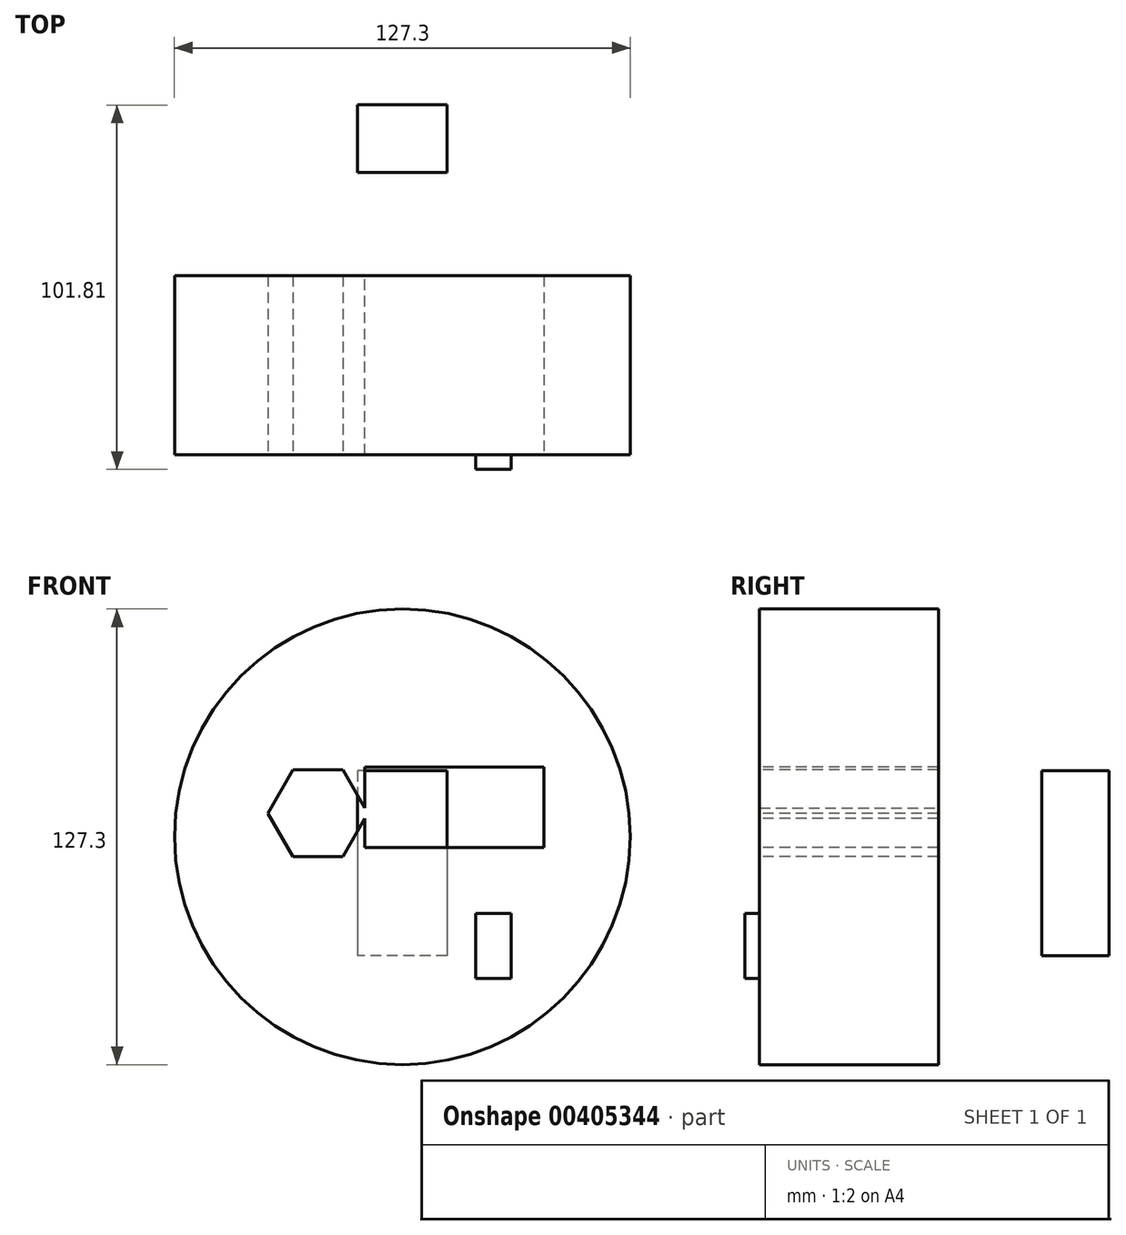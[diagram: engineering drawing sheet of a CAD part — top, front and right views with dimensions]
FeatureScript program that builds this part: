
annotation { "Feature Type Name" : "Feature", "Feature Type Description" : "" }
export const myFeature = defineFeature(function(context is Context, id is Id, definition is map)
    precondition{}
    {
        {
            var Q0;
            Q0=qCreatedBy(makeId("Front.planeOp"),FACE);
            var sketch = newSketch(context, id + "F0", { "sketchPlane" : qUnion([Q0])});
            skCircle(sketch, "E0", {"center": v(0, 0) * mm, "radius": 63.65 * mm});
            skSolve(sketch);
        }
        {
            var Q0;
            Q0=makeQuery(id+"F0.imprint","IMPRINT",FACE,{"disambiguationData":[TD([[makeQuery(id+"F0.imprint","IMPRINT",EDGE,{"derivedFrom":sQuery(id+"F0.wireOp",EDGE,"E0")}),1.0]])]});
            extrude(context, id + "F1", {"entities" : qUnion([Q0]), "endBound" : BoundingType.SYMMETRIC, "depth" : 50 * mm});
        }
        {
            var Q0;
            Q0=makeQuery(id+"F1.opExtrude","CAP_FACE",FACE,{"disambiguationData":[OSD([sQuery(id+"F0.wireOp",EDGE,"E0")])],"isStart":false});
            var sketch = newSketch(context, id + "F2", { "sketchPlane" : qUnion([Q0])});
            skLineSegment(sketch, "E1.bottom", {"start": v(-10.5, 19.5) * mm, "end": v(39.5, 19.5) * mm});
            skLineSegment(sketch, "E1.top", {"start": v(-10.5, -3.05) * mm, "end": v(39.5, -3.05) * mm});
            skLineSegment(sketch, "E1.left", {"start": v(39.5, -3.05) * mm, "end": v(39.5, 19.5) * mm});
            skLineSegment(sketch, "E1.right", {"start": v(-10.5, -3.05) * mm, "end": v(-10.5, 19.5) * mm});
            skPoint(sketch, "E1.middle", {"position": v(14.5, 8.23) * mm});
            skSolve(sketch);
        }
        {
            var Q0;
            Q0=makeQuery(id+"F2.imprint","IMPRINT",FACE,{"disambiguationData":[TD([[makeQuery(id+"F2.imprint","IMPRINT",EDGE,{"derivedFrom":sQuery(id+"F2.wireOp",EDGE,"E1.bottom")}),-1.0]])]});
            extrude(context, id + "F3", {"entities" : qUnion([Q0]), "operationType" : NewBodyOperationType.REMOVE, "oppositeDirection" : true, "depth" : 100 * mm});
        }
        {
            var Q0;
            Q0=makeQuery(id+"F1.opExtrude","CAP_FACE",FACE,{"disambiguationData":[OSD([sQuery(id+"F0.wireOp",EDGE,"E0")])],"isStart":false});
            var sketch = newSketch(context, id + "F4", { "sketchPlane" : qUnion([Q0])});
            skCircle(sketch, "E2.cCircle", {"center": v(-23.62, 6.57) * mm, "radius": 12.11 * mm, "construction": true});
            skLineSegment(sketch, "E2.0", {"start": v(-30.61, 18.68) * mm, "end": v(-16.63, 18.68) * mm});
            skLineSegment(sketch, "E2.1", {"start": v(-16.63, 18.68) * mm, "end": v(-9.64, 6.57) * mm});
            skLineSegment(sketch, "E2.2", {"start": v(-9.64, 6.57) * mm, "end": v(-16.63, -5.54) * mm});
            skLineSegment(sketch, "E2.3", {"start": v(-16.63, -5.54) * mm, "end": v(-30.61, -5.54) * mm});
            skLineSegment(sketch, "E2.4", {"start": v(-30.61, -5.54) * mm, "end": v(-37.6, 6.57) * mm});
            skLineSegment(sketch, "E2.5", {"start": v(-37.6, 6.57) * mm, "end": v(-30.61, 18.68) * mm});
            skPoint(sketch, "E2.0.midPoint", {"position": v(-23.62, 18.68) * mm});
            skSolve(sketch);
        }
        {
            var Q0;
            Q0 = qSketchRegion(id + "F4", true);
            extrude(context, id + "F5", {"entities" : qUnion([Q0]), "operationType" : NewBodyOperationType.REMOVE, "oppositeDirection" : true, "depth" : 60 * mm});
        }
        {
            var Q0;
            Q0=makeQuery(id+"F1.opExtrude","CAP_FACE",FACE,{"disambiguationData":[OSD([sQuery(id+"F0.wireOp",EDGE,"E0")])],"isStart":false});
            var sketch = newSketch(context, id + "F6", { "sketchPlane" : qUnion([Q0])});
            skLineSegment(sketch, "E3.bottom", {"start": v(30.34, -39.6) * mm, "end": v(20.49, -39.6) * mm});
            skLineSegment(sketch, "E3.top", {"start": v(30.34, -21.43) * mm, "end": v(20.49, -21.43) * mm});
            skLineSegment(sketch, "E3.left", {"start": v(30.34, -39.6) * mm, "end": v(30.34, -21.43) * mm});
            skLineSegment(sketch, "E3.right", {"start": v(20.49, -39.6) * mm, "end": v(20.49, -21.43) * mm});
            skPoint(sketch, "E4.firstSnap0", {"position": v(30.34, -30.5) * mm});
            skPoint(sketch, "E4.oppositeSnap0", {"position": v(30.34, -30.5) * mm});
            skSolve(sketch);
        }
        {
            var Q0;
            Q0=makeQuery(id+"F6.imprint","IMPRINT",FACE,{"disambiguationData":[TD([[makeQuery(id+"F6.imprint","IMPRINT",EDGE,{"derivedFrom":sQuery(id+"F6.wireOp",EDGE,"E3.bottom")}),-1.0]])]});
            extrude(context, id + "F7", {"entities" : qUnion([Q0]), "depth" : 4.08 * mm});
        }
        {
            var Q0;
            Q0=qCreatedBy(makeId("Right.planeOp"),FACE);
            var sketch = newSketch(context, id + "F8", { "sketchPlane" : qUnion([Q0])});
            skLineSegment(sketch, "E5.top", {"start": v(53.92, -33.16) * mm, "end": v(72.73, -33.16) * mm});
            skLineSegment(sketch, "E5.left", {"start": v(53.92, 18.44) * mm, "end": v(53.92, -33.16) * mm});
            skLineSegment(sketch, "E5.right", {"start": v(72.73, 18.44) * mm, "end": v(72.73, -33.16) * mm});
            skPoint(sketch, "E5.middle", {"position": v(63.33, -7.36) * mm});
            skLineSegment(sketch, "E6", {"start": v(53.92, 18.44) * mm, "end": v(72.73, 18.44) * mm});
            skSolve(sketch);
        }
        {
            var Q0;
            Q0=makeQuery(id+"F8.imprint","IMPRINT",FACE,{"disambiguationData":[TD([[makeQuery(id+"F8.imprint","IMPRINT",EDGE,{"derivedFrom":sQuery(id+"F8.wireOp",EDGE,"E5.top")}),1.0]])]});
            extrude(context, id + "F9", {"entities" : qUnion([Q0]), "endBound" : BoundingType.SYMMETRIC, "depth" : 25 * mm});
        }
    });
